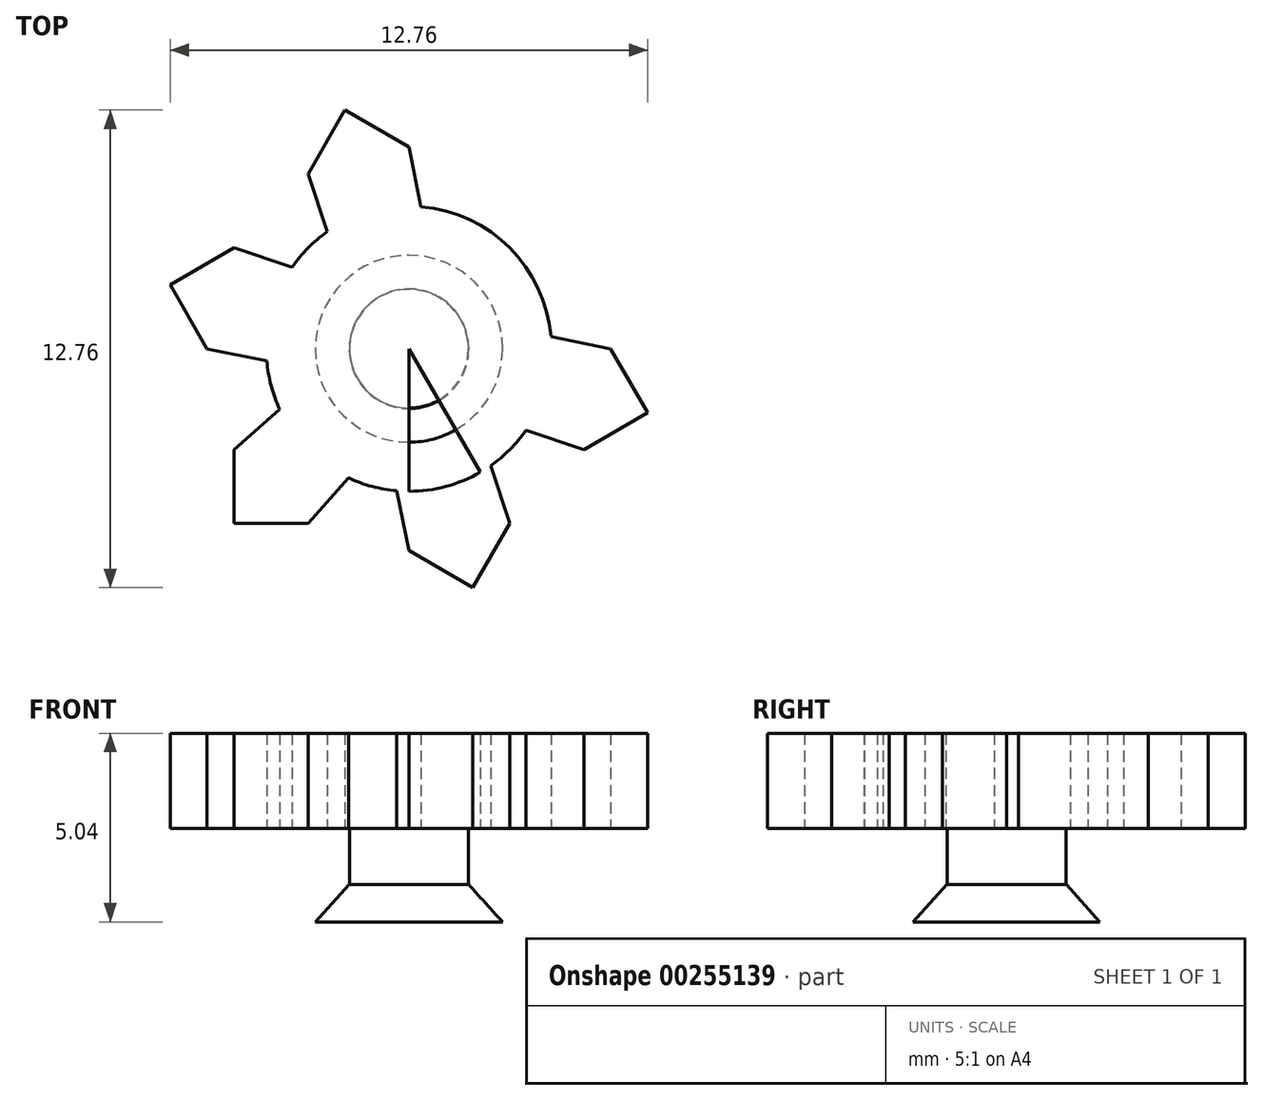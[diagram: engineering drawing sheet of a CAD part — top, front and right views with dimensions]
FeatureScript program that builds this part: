
annotation { "Feature Type Name" : "Feature", "Feature Type Description" : "" }
export const myFeature = defineFeature(function(context is Context, id is Id, definition is map)
    precondition{}
    {
        {
            var Q0;
            Q0=qCreatedBy(makeId("Top.planeOp"),FACE);
            var sketch = newSketch(context, id + "F0", { "sketchPlane" : qUnion([Q0])});
            skLineSegment(sketch, "E0", {"start": v(0, 3.81) * mm, "end": v(0, -6.35) * mm});
            skLineSegment(sketch, "E1.1.0", {"start": v(1.9, 3.3) * mm, "end": v(-1.9, -3.3) * mm});
            skLineSegment(sketch, "E1.2.0", {"start": v(3.3, 1.9) * mm, "end": v(-3.3, -1.9) * mm});
            skLineSegment(sketch, "E1.3.0", {"start": v(3.81, 0) * mm, "end": v(-3.81, 0) * mm});
            skLineSegment(sketch, "E1.4.0", {"start": v(3.3, -1.9) * mm, "end": v(-3.3, 1.9) * mm});
            skLineSegment(sketch, "E1.5.0", {"start": v(1.9, -3.3) * mm, "end": v(-1.9, 3.3) * mm});
            skPoint(sketch, "E1.center", {"position": v(0, 0) * mm});
            skLineSegment(sketch, "E1.anchor1", {"start": v(0, 0) * mm, "end": v(0, -3.81) * mm, "construction": true});
            skLineSegment(sketch, "E1.anchor2", {"start": v(0, 0) * mm, "end": v(-1.9, 3.3) * mm, "construction": true});
            skCircle(sketch, "E2", {"center": v(0, 0) * mm, "radius": 3.81 * mm});
            skLineSegment(sketch, "E3", {"start": v(4.67, 4.67) * mm, "end": v(4.67, 2.7) * mm});
            skLineSegment(sketch, "E4", {"start": v(4.67, 2.7) * mm, "end": v(4.67, 4.67) * mm});
            skLineSegment(sketch, "E5", {"start": v(4.67, 4.67) * mm, "end": v(2.7, 4.67) * mm});
            skLineSegment(sketch, "E6", {"start": v(2.7, 4.67) * mm, "end": v(1.62, 3.45) * mm});
            skLineSegment(sketch, "E7", {"start": v(1.62, 3.45) * mm, "end": v(2.7, 4.67) * mm});
            skLineSegment(sketch, "E8", {"start": v(4.67, 2.7) * mm, "end": v(3.45, 1.62) * mm});
            skPoint(sketch, "E9.orphan", {"position": v(5.5, 3.18) * mm});
            skPoint(sketch, "E10.orphan", {"position": v(5.83, 3.5) * mm});
            skPoint(sketch, "E11.2.start.orphan", {"position": v(3.5, 5.83) * mm});
            skPoint(sketch, "E12.orphan", {"position": v(3.18, 5.5) * mm});
            skPoint(sketch, "E13.orphan", {"position": v(-3.17, 5.5) * mm});
            skPoint(sketch, "E14.orphan", {"position": v(0, 6.35) * mm});
            skPoint(sketch, "E15.orphan", {"position": v(-5.5, 3.18) * mm});
            skPoint(sketch, "E16.orphan", {"position": v(-6.35, 0) * mm});
            skPoint(sketch, "E17.orphan", {"position": v(-5.5, -3.18) * mm});
            skPoint(sketch, "E18.orphan", {"position": v(-3.18, -5.5) * mm});
            skPoint(sketch, "E19.orphan", {"position": v(3.17, -5.5) * mm});
            skPoint(sketch, "E20.orphan", {"position": v(5.5, -3.18) * mm});
            skPoint(sketch, "E21.orphan", {"position": v(6.35, 0) * mm});
            skLineSegment(sketch, "E22.1.0", {"start": v(0, 5.4) * mm, "end": v(-1.7, 6.38) * mm});
            skLineSegment(sketch, "E22.1.1", {"start": v(0, 5.4) * mm, "end": v(0.32, 3.8) * mm});
            skLineSegment(sketch, "E22.1.2", {"start": v(-1.7, 6.38) * mm, "end": v(-2.7, 4.67) * mm});
            skLineSegment(sketch, "E22.1.3", {"start": v(-2.7, 4.67) * mm, "end": v(-2.18, 3.13) * mm});
            skLineSegment(sketch, "E22.2.0", {"start": v(-4.67, 2.7) * mm, "end": v(-6.38, 1.7) * mm});
            skLineSegment(sketch, "E22.2.1", {"start": v(-4.67, 2.7) * mm, "end": v(-3.13, 2.18) * mm});
            skLineSegment(sketch, "E22.2.2", {"start": v(-6.38, 1.7) * mm, "end": v(-5.4, 0) * mm});
            skLineSegment(sketch, "E22.2.3", {"start": v(-5.4, 0) * mm, "end": v(-3.8, -0.32) * mm});
            skLineSegment(sketch, "E22.3.0", {"start": v(-4.67, -2.7) * mm, "end": v(-4.67, -4.67) * mm});
            skLineSegment(sketch, "E22.3.1", {"start": v(-4.67, -2.7) * mm, "end": v(-3.45, -1.62) * mm});
            skLineSegment(sketch, "E22.3.2", {"start": v(-4.67, -4.67) * mm, "end": v(-2.7, -4.67) * mm});
            skLineSegment(sketch, "E22.3.3", {"start": v(-2.7, -4.67) * mm, "end": v(-1.62, -3.45) * mm});
            skLineSegment(sketch, "E22.4.0", {"start": v(0, -5.4) * mm, "end": v(1.7, -6.38) * mm});
            skLineSegment(sketch, "E22.4.1", {"start": v(0, -5.4) * mm, "end": v(-0.32, -3.8) * mm});
            skLineSegment(sketch, "E22.4.2", {"start": v(1.7, -6.38) * mm, "end": v(2.7, -4.67) * mm});
            skLineSegment(sketch, "E22.4.3", {"start": v(2.7, -4.67) * mm, "end": v(2.18, -3.13) * mm});
            skLineSegment(sketch, "E22.5.0", {"start": v(4.67, -2.7) * mm, "end": v(6.38, -1.7) * mm});
            skLineSegment(sketch, "E22.5.1", {"start": v(4.67, -2.7) * mm, "end": v(3.13, -2.18) * mm});
            skLineSegment(sketch, "E22.5.2", {"start": v(6.38, -1.7) * mm, "end": v(5.4, 0) * mm});
            skLineSegment(sketch, "E22.5.3", {"start": v(5.4, 0) * mm, "end": v(3.8, 0.32) * mm});
            skCircle(sketch, "E23", {"center": v(0, 0) * mm, "radius": 6.6 * mm});
            skSolve(sketch);
        }
        {
            var Q0;
            Q0=makeQuery(id+"F0.imprint","IMPRINT",FACE,{"disambiguationData":[TD([[makeQuery(id+"F0.imprint","IMPRINT",EDGE,{"derivedFrom":sQuery(id+"F0.wireOp",EDGE,"E4")}),1.0]])]});
            var Q1;
            {var subQ0=sQuery(id+"F0.wireOp",EDGE,"E2");var subQ1=sQuery(id+"F0.wireOp",EDGE,"E1.1.0");var subQ2=makeQuery(id+"F0.imprint","INTERSECT",VERTEX,{"disambiguationData":[OD(0.0)],"derivedFrom":[subQ1,subQ0]});Q1=makeQuery(id+"F0.imprint","IMPRINT",FACE,{"disambiguationData":[TD([[makeQuery(id+"F0.imprint","IMPRINT",EDGE,{"disambiguationData":[TD([[subQ2,1.0]])],"derivedFrom":subQ0}),1.0]])]});}
            var Q2;
            {var subQ0=sQuery(id+"F0.wireOp",EDGE,"E2");var subQ3=sQuery(id+"F0.wireOp",EDGE,"E1.1.0");var subQ4=makeQuery(id+"F0.imprint","INTERSECT",VERTEX,{"disambiguationData":[OD(0.0)],"derivedFrom":[subQ3,subQ0]});Q2=makeQuery(id+"F0.imprint","IMPRINT",FACE,{"disambiguationData":[TD([[makeQuery(id+"F0.imprint","IMPRINT",EDGE,{"disambiguationData":[TD([[subQ4,-1.0]])],"derivedFrom":subQ0}),1.0]])]});}
            var Q3;
            Q3=makeQuery(id+"F0.imprint","IMPRINT",FACE,{"disambiguationData":[TD([[makeQuery(id+"F0.imprint","IMPRINT",EDGE,{"derivedFrom":sQuery(id+"F0.wireOp",EDGE,"E22.1.0")}),1.0]])]});
            var Q4;
            {var subQ0=sQuery(id+"F0.wireOp",EDGE,"E2");var subQ1=sQuery(id+"F0.wireOp",EDGE,"E0");var subQ2=makeQuery(id+"F0.imprint","INTERSECT",VERTEX,{"disambiguationData":[OD(0.0)],"derivedFrom":[subQ1,subQ0]});Q4=makeQuery(id+"F0.imprint","IMPRINT",FACE,{"disambiguationData":[TD([[makeQuery(id+"F0.imprint","IMPRINT",EDGE,{"disambiguationData":[TD([[subQ2,-1.0]])],"derivedFrom":subQ0}),1.0]])]});}
            var Q5;
            {var subQ0=sQuery(id+"F0.wireOp",EDGE,"E2");var subQ5=sQuery(id+"F0.wireOp",EDGE,"E1.5.0");var subQ6=makeQuery(id+"F0.imprint","INTERSECT",VERTEX,{"disambiguationData":[OD(1.0)],"derivedFrom":[subQ5,subQ0]});Q5=makeQuery(id+"F0.imprint","IMPRINT",FACE,{"disambiguationData":[TD([[makeQuery(id+"F0.imprint","IMPRINT",EDGE,{"disambiguationData":[TD([[subQ6,-1.0]])],"derivedFrom":subQ0}),1.0]])]});}
            var Q6;
            Q6=makeQuery(id+"F0.imprint","IMPRINT",FACE,{"disambiguationData":[TD([[makeQuery(id+"F0.imprint","IMPRINT",EDGE,{"derivedFrom":sQuery(id+"F0.wireOp",EDGE,"E22.2.0")}),1.0]])]});
            var Q7;
            {var subQ0=sQuery(id+"F0.wireOp",EDGE,"E2");var subQ1=sQuery(id+"F0.wireOp",EDGE,"E1.3.0");var subQ2=makeQuery(id+"F0.imprint","INTERSECT",VERTEX,{"disambiguationData":[OD(1.0)],"derivedFrom":[subQ1,subQ0]});Q7=makeQuery(id+"F0.imprint","IMPRINT",FACE,{"disambiguationData":[TD([[makeQuery(id+"F0.imprint","IMPRINT",EDGE,{"disambiguationData":[TD([[subQ2,1.0]])],"derivedFrom":subQ0}),1.0]])]});}
            var Q8;
            {var subQ0=sQuery(id+"F0.wireOp",EDGE,"E2");var subQ3=sQuery(id+"F0.wireOp",EDGE,"E1.3.0");var subQ4=makeQuery(id+"F0.imprint","INTERSECT",VERTEX,{"disambiguationData":[OD(1.0)],"derivedFrom":[subQ3,subQ0]});Q8=makeQuery(id+"F0.imprint","IMPRINT",FACE,{"disambiguationData":[TD([[makeQuery(id+"F0.imprint","IMPRINT",EDGE,{"disambiguationData":[TD([[subQ4,-1.0]])],"derivedFrom":subQ0}),1.0]])]});}
            var Q9;
            {var subQ0=sQuery(id+"F0.wireOp",EDGE,"E2");var subQ1=sQuery(id+"F0.wireOp",EDGE,"E1.1.0");var subQ2=makeQuery(id+"F0.imprint","INTERSECT",VERTEX,{"disambiguationData":[OD(1.0)],"derivedFrom":[subQ1,subQ0]});Q9=makeQuery(id+"F0.imprint","IMPRINT",FACE,{"disambiguationData":[TD([[makeQuery(id+"F0.imprint","IMPRINT",EDGE,{"disambiguationData":[TD([[subQ2,1.0]])],"derivedFrom":subQ0}),1.0]])]});}
            var Q10;
            Q10=makeQuery(id+"F0.imprint","IMPRINT",FACE,{"disambiguationData":[TD([[makeQuery(id+"F0.imprint","IMPRINT",EDGE,{"derivedFrom":sQuery(id+"F0.wireOp",EDGE,"E22.3.0")}),1.0]])]});
            var Q11;
            {var subQ0=sQuery(id+"F0.wireOp",EDGE,"E2");var subQ3=sQuery(id+"F0.wireOp",EDGE,"E1.1.0");var subQ4=makeQuery(id+"F0.imprint","INTERSECT",VERTEX,{"disambiguationData":[OD(1.0)],"derivedFrom":[subQ3,subQ0]});Q11=makeQuery(id+"F0.imprint","IMPRINT",FACE,{"disambiguationData":[TD([[makeQuery(id+"F0.imprint","IMPRINT",EDGE,{"disambiguationData":[TD([[subQ4,-1.0]])],"derivedFrom":subQ0}),1.0]])]});}
            var Q12;
            {var subQ0=sQuery(id+"F0.wireOp",EDGE,"E22.4.0");Q12=makeQuery(id+"F0.imprint","IMPRINT",FACE,{"disambiguationData":[TD([[makeQuery(id+"F0.imprint","IMPRINT",EDGE,{"derivedFrom":subQ0}),1.0]])]});}
            var Q13;
            {var subQ0=sQuery(id+"F0.wireOp",EDGE,"E2");var subQ3=sQuery(id+"F0.wireOp",EDGE,"E1.5.0");var subQ5=makeQuery(id+"F0.imprint","INTERSECT",VERTEX,{"disambiguationData":[OD(0.0)],"derivedFrom":[subQ3,subQ0]});Q13=makeQuery(id+"F0.imprint","IMPRINT",FACE,{"disambiguationData":[TD([[makeQuery(id+"F0.imprint","IMPRINT",EDGE,{"disambiguationData":[TD([[subQ5,1.0]])],"derivedFrom":subQ0}),1.0]])]});}
            var Q14;
            {var subQ0=sQuery(id+"F0.wireOp",EDGE,"E2");var subQ3=sQuery(id+"F0.wireOp",EDGE,"E1.5.0");var subQ4=makeQuery(id+"F0.imprint","INTERSECT",VERTEX,{"disambiguationData":[OD(0.0)],"derivedFrom":[subQ3,subQ0]});Q14=makeQuery(id+"F0.imprint","IMPRINT",FACE,{"disambiguationData":[TD([[makeQuery(id+"F0.imprint","IMPRINT",EDGE,{"disambiguationData":[TD([[subQ4,-1.0]])],"derivedFrom":subQ0}),1.0]])]});}
            var Q15;
            {var subQ0=sQuery(id+"F0.wireOp",EDGE,"E2");var subQ1=sQuery(id+"F0.wireOp",EDGE,"E1.3.0");var subQ2=makeQuery(id+"F0.imprint","INTERSECT",VERTEX,{"disambiguationData":[OD(0.0)],"derivedFrom":[subQ1,subQ0]});Q15=makeQuery(id+"F0.imprint","IMPRINT",FACE,{"disambiguationData":[TD([[makeQuery(id+"F0.imprint","IMPRINT",EDGE,{"disambiguationData":[TD([[subQ2,1.0]])],"derivedFrom":subQ0}),1.0]])]});}
            var Q16;
            {var subQ0=sQuery(id+"F0.wireOp",EDGE,"E2");var subQ3=sQuery(id+"F0.wireOp",EDGE,"E1.3.0");var subQ4=makeQuery(id+"F0.imprint","INTERSECT",VERTEX,{"disambiguationData":[OD(0.0)],"derivedFrom":[subQ3,subQ0]});Q16=makeQuery(id+"F0.imprint","IMPRINT",FACE,{"disambiguationData":[TD([[makeQuery(id+"F0.imprint","IMPRINT",EDGE,{"disambiguationData":[TD([[subQ4,-1.0]])],"derivedFrom":subQ0}),1.0]])]});}
            var Q17;
            Q17=makeQuery(id+"F0.imprint","IMPRINT",FACE,{"disambiguationData":[TD([[makeQuery(id+"F0.imprint","IMPRINT",EDGE,{"derivedFrom":sQuery(id+"F0.wireOp",EDGE,"E22.5.0")}),1.0]])]});
            var Q18;
            {var subQ0=sQuery(id+"F0.wireOp",EDGE,"E22.4.1");Q18=makeQuery(id+"F0.imprint","IMPRINT",FACE,{"disambiguationData":[TD([[makeQuery(id+"F0.imprint","IMPRINT",EDGE,{"derivedFrom":subQ0}),-1.0]])]});}
            extrude(context, id + "F1", {"entities" : qUnion([Q0, Q1, Q2, Q3, Q4, Q5, Q6, Q7, Q8, Q9, Q10, Q11, Q12, Q13, Q14, Q15, Q16, Q17, Q18]), "depth" : 2.54 * mm});
        }
        {
            var Q0;
            Q0=makeQuery(id+"F1.opExtrude","CAP_FACE",FACE,{"disambiguationData":[OSD([sQuery(id+"F0.wireOp",EDGE,"E2"),sQuery(id+"F0.wireOp",EDGE,"E4"),sQuery(id+"F0.wireOp",EDGE,"E5"),sQuery(id+"F0.wireOp",EDGE,"E7"),sQuery(id+"F0.wireOp",EDGE,"E8"),sQuery(id+"F0.wireOp",EDGE,"E22.1.0"),sQuery(id+"F0.wireOp",EDGE,"E22.1.1"),sQuery(id+"F0.wireOp",EDGE,"E22.1.2"),sQuery(id+"F0.wireOp",EDGE,"E22.1.3"),sQuery(id+"F0.wireOp",EDGE,"E22.2.0"),sQuery(id+"F0.wireOp",EDGE,"E22.2.1"),sQuery(id+"F0.wireOp",EDGE,"E22.2.2"),sQuery(id+"F0.wireOp",EDGE,"E22.2.3"),sQuery(id+"F0.wireOp",EDGE,"E22.3.0"),sQuery(id+"F0.wireOp",EDGE,"E22.3.1"),sQuery(id+"F0.wireOp",EDGE,"E22.3.2"),sQuery(id+"F0.wireOp",EDGE,"E22.3.3"),sQuery(id+"F0.wireOp",EDGE,"E22.4.0"),sQuery(id+"F0.wireOp",EDGE,"E22.4.1"),sQuery(id+"F0.wireOp",EDGE,"E22.4.2"),sQuery(id+"F0.wireOp",EDGE,"E22.4.3"),sQuery(id+"F0.wireOp",EDGE,"E22.5.0"),sQuery(id+"F0.wireOp",EDGE,"E22.5.1"),sQuery(id+"F0.wireOp",EDGE,"E22.5.2"),sQuery(id+"F0.wireOp",EDGE,"E22.5.3")])],"isStart":true});
            var sketch = newSketch(context, id + "F2", { "sketchPlane" : qUnion([Q0])});
            skCircle(sketch, "E24", {"center": v(0, 0) * mm, "radius": 1.59 * mm});
            skSolve(sketch);
        }
        {
            var Q0;
            Q0 = qSketchRegion(id + "F2", true);
            extrude(context, id + "F3", {"entities" : qUnion([Q0]), "operationType" : NewBodyOperationType.ADD, "depth" : 1.5 * mm});
        }
        {
            var Q0;
            Q0=makeQuery(id+"F3.opExtrude","CAP_FACE",FACE,{"disambiguationData":[OSD([sQuery(id+"F2.wireOp",EDGE,"E24")])],"isStart":false});
            var sketch = newSketch(context, id + "F4", { "sketchPlane" : qUnion([Q0])});
            skCircle(sketch, "E25", {"center": v(0, 0) * mm, "radius": 2.5 * mm});
            skSolve(sketch);
        }
        {
            var Q0;
            Q0 = qSketchRegion(id + "F4", true);
            extrude(context, id + "F5", {"entities" : qUnion([Q0]), "operationType" : NewBodyOperationType.ADD, "depth" : 1 * mm});
        }
        {
            var Q0;
            Q0=qCreatedBy(makeId("Right.planeOp"),FACE);
            var sketch = newSketch(context, id + "F6", { "sketchPlane" : qUnion([Q0])});
            skLineSegment(sketch, "E26", {"start": v(0, 0) * mm, "end": v(0, -2.5) * mm});
            skLineSegment(sketch, "E27", {"start": v(0, -2.5) * mm, "end": v(2.5, -2.5) * mm});
            skLineSegment(sketch, "E28", {"start": v(2.5, -2.5) * mm, "end": v(0, -2.5) * mm});
            skLineSegment(sketch, "E29", {"start": v(0, -2.5) * mm, "end": v(0, -1.5) * mm});
            skLineSegment(sketch, "E30", {"start": v(0, -1.5) * mm, "end": v(1.7, -1.5) * mm});
            skLineSegment(sketch, "E31", {"start": v(1.7, -1.5) * mm, "end": v(2.5, -1.5) * mm});
            skLineSegment(sketch, "E32", {"start": v(2.5, -1.5) * mm, "end": v(2.5, -2.5) * mm});
            skLineSegment(sketch, "E33", {"start": v(1.6, -1.5) * mm, "end": v(2.5, -2.5) * mm});
            skSolve(sketch);
        }
        {
            var Q0;
            {var subQ0=sQuery(id+"F6.wireOp",EDGE,"E31");Q0=makeQuery(id+"F6.imprint","IMPRINT",FACE,{"disambiguationData":[TD([[makeQuery(id+"F6.imprint","IMPRINT",EDGE,{"derivedFrom":subQ0}),-1.0]])]});}
            var Q1;
            Q1=sQuery(id+"F6.wireOp",EDGE,"E29");
            revolve(context, id + "F7", {"operationType" : NewBodyOperationType.REMOVE, "entities" : qUnion([Q0]), "axis" : qUnion([Q1]), "revolveType" : RevolveType.FULL, "oppositeDirection" : true});
        }
    });
